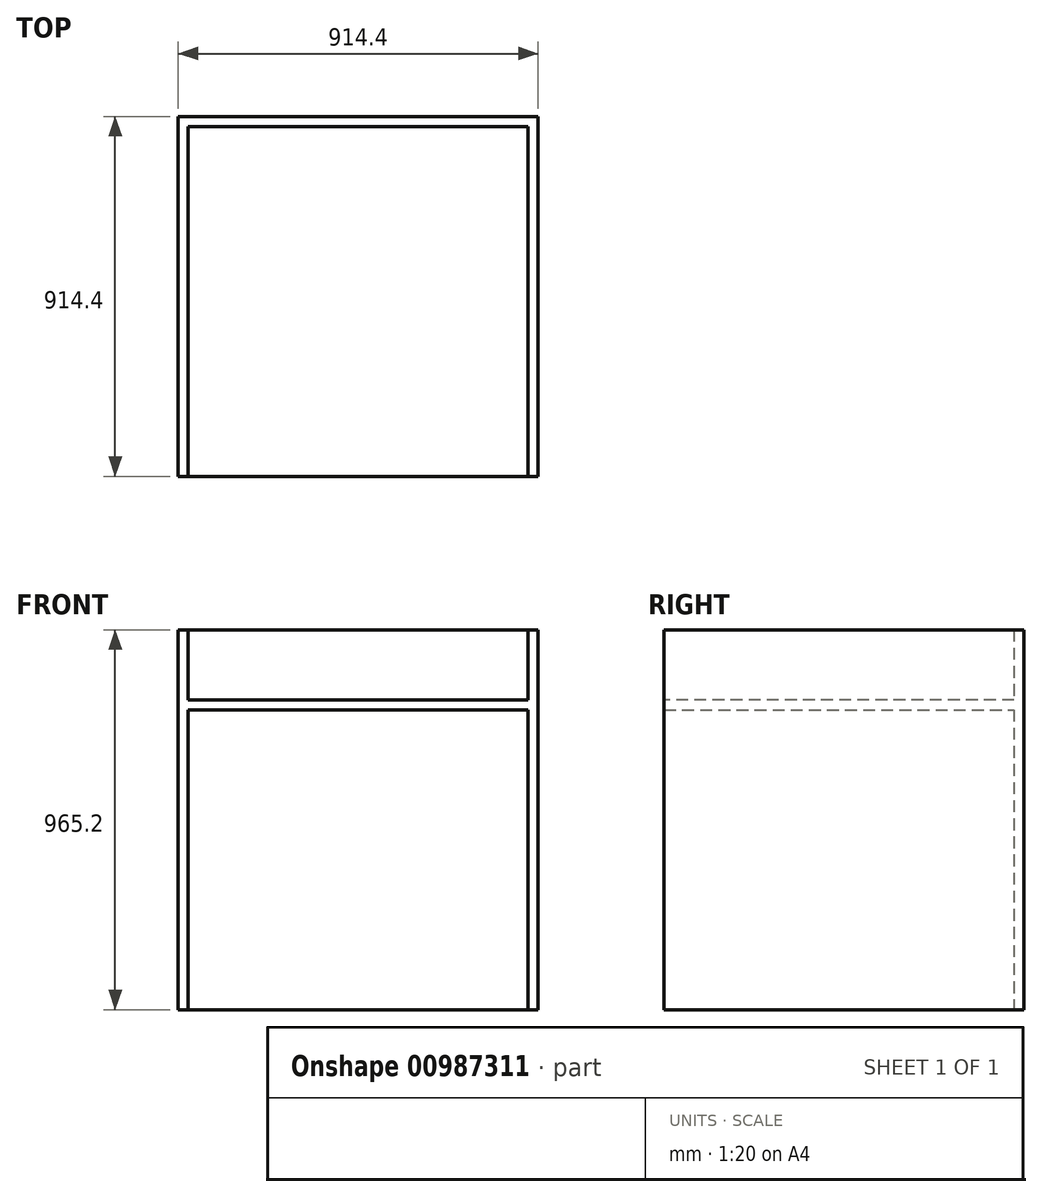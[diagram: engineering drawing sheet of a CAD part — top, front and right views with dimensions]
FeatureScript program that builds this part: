
annotation { "Feature Type Name" : "Feature", "Feature Type Description" : "" }
export const myFeature = defineFeature(function(context is Context, id is Id, definition is map)
    precondition{}
    {
        {
            var Q0;
            Q0=qCreatedBy(makeId("Top.planeOp"),FACE);
            var sketch = newSketch(context, id + "F0", { "sketchPlane" : qUnion([Q0])});
            skLineSegment(sketch, "E0.top", {"start": v(0, 914.4) * mm, "end": v(914.4, 914.4) * mm});
            skLineSegment(sketch, "E0.left", {"start": v(0, 0) * mm, "end": v(0, 914.4) * mm});
            skLineSegment(sketch, "E0.right", {"start": v(914.4, 0) * mm, "end": v(914.4, 914.4) * mm});
            skLineSegment(sketch, "E1.bottom", {"start": v(0, 0) * mm, "end": v(25.4, 0) * mm});
            skLineSegment(sketch, "E1.left", {"start": v(0, 0) * mm, "end": v(0, 25.4) * mm});
            skLineSegment(sketch, "E1.right", {"start": v(25.4, 0) * mm, "end": v(25.4, 25.4) * mm});
            skLineSegment(sketch, "E2.bottom", {"start": v(914.4, 914.4) * mm, "end": v(889, 914.4) * mm});
            skLineSegment(sketch, "E2.left", {"start": v(914.4, 914.4) * mm, "end": v(914.4, 889) * mm});
            skLineSegment(sketch, "E3.top", {"start": v(25.4, 889) * mm, "end": v(889, 889) * mm});
            skLineSegment(sketch, "E3.left", {"start": v(25.4, 25.4) * mm, "end": v(25.4, 889) * mm});
            skLineSegment(sketch, "E3.right", {"start": v(889, 25.4) * mm, "end": v(889, 889) * mm});
            skLineSegment(sketch, "E4", {"start": v(889, 25.4) * mm, "end": v(889, 0) * mm});
            skLineSegment(sketch, "E5", {"start": v(889, 0) * mm, "end": v(914.4, 0) * mm});
            skSolve(sketch);
        }
        {
            var Q0;
            Q0=makeQuery(id+"F0.imprint","IMPRINT",FACE,{"disambiguationData":[TD([[makeQuery(id+"F0.imprint","IMPRINT",EDGE,{"derivedFrom":sQuery(id+"F0.wireOp",EDGE,"E0.top")}),-1.0]])]});
            extrude(context, id + "F1", {"entities" : qUnion([Q0]), "depth" : 914.4 * mm, "offsetDistance" : 25.4 * mm});
        }
        {
            var Q0;
            Q0=makeQuery(id+"F1.opExtrude","SWEPT_FACE",FACE,{"disambiguationData":[OSD([sQuery(id+"F0.wireOp",EDGE,"E3.right"),sQuery(id+"F0.wireOp",EDGE,"E4")])]});
            var sketch = newSketch(context, id + "F2", { "sketchPlane" : qUnion([Q0])});
            skLineSegment(sketch, "E6.top", {"start": v(0, 762) * mm, "end": v(-889, 762) * mm});
            skLineSegment(sketch, "E7.top", {"start": v(0, 787.4) * mm, "end": v(-889, 787.4) * mm});
            skLineSegment(sketch, "E7.left", {"start": v(0, 762) * mm, "end": v(0, 787.4) * mm});
            skLineSegment(sketch, "E7.right", {"start": v(-889, 762) * mm, "end": v(-889, 787.4) * mm});
            skSolve(sketch);
        }
        {
            var Q0;
            Q0=makeQuery(id+"F2.imprint","IMPRINT",FACE,{"disambiguationData":[TD([[makeQuery(id+"F2.imprint","IMPRINT",EDGE,{"derivedFrom":sQuery(id+"F2.wireOp",EDGE,"E6.top")}),-1.0]])]});
            extrude(context, id + "F3", {"entities" : qUnion([Q0]), "operationType" : NewBodyOperationType.ADD, "depth" : 889 * mm, "offsetDistance" : 25.4 * mm});
        }
        {
            var Q0;
            Q0=makeQuery(id+"F1.opExtrude","CAP_FACE",FACE,{"disambiguationData":[OSD([sQuery(id+"F0.wireOp",EDGE,"E0.top"),sQuery(id+"F0.wireOp",EDGE,"E0.left"),sQuery(id+"F0.wireOp",EDGE,"E0.right"),sQuery(id+"F0.wireOp",EDGE,"E1.bottom"),sQuery(id+"F0.wireOp",EDGE,"E1.left"),sQuery(id+"F0.wireOp",EDGE,"E1.right"),sQuery(id+"F0.wireOp",EDGE,"E2.bottom"),sQuery(id+"F0.wireOp",EDGE,"E2.left"),sQuery(id+"F0.wireOp",EDGE,"E3.top"),sQuery(id+"F0.wireOp",EDGE,"E3.left"),sQuery(id+"F0.wireOp",EDGE,"E3.right"),sQuery(id+"F0.wireOp",EDGE,"E4"),sQuery(id+"F0.wireOp",EDGE,"E5")])],"isStart":false});
            extrude(context, id + "F4", {"entities" : qUnion([Q0]), "operationType" : NewBodyOperationType.ADD, "depth" : 50.8 * mm, "offsetDistance" : 25.4 * mm});
        }
    });
